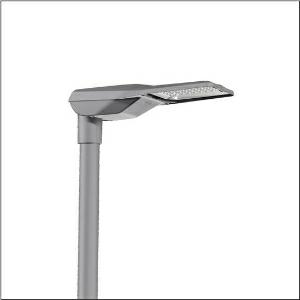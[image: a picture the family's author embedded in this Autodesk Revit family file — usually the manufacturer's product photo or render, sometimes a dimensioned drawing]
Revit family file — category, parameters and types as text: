
# Revit family: streetlight_sl_21_iq_mini___st1_0a_5xe2d31g08gb_f91a
name_source: partatom
category: Lighting Fixtures
units: mm (PartAtom-declared; Revit-internal decimal feet)

## family parameters
Cut with Voids When Loaded = No
Host = Face
Light Source = No
Part Type = Normal
Room Calculation Point = No
Round Connector Dimension = Use Diameter
Shared = No

## types (1)
- --- (1 x LED, 5680 lm, 37.1 W, 3000K)
    Apparent Load = 37 VA
    CIE Flux Codes = 37 72 97 100 100
    Color Rendering = 70
    Color Temperature = 3000K
    Default Elevation = 1800 mm
    Description = Streetlight SL 21 mini, mast luminaire, primary light control with lens, of PMMA, primary optical cover: cover, of toughened safety glass, transparent, light distribution: ST1.0a, light emission: direct distribution, primary light characteristic: asymmetric, installation type: post-top, side-entry, LED, High Power LED, rated luminous flux: 5.680lm, luminous efficacy: 153lm/W, light colour: 730, colour temperature: 3000K, control gear: ECG iQ, control: Street-Remote, Auto-Match, Temp-Guard, Lumen-Switch, Night-Set, Smart-Wire, Light-Fading, Desk-Remote (wireless, voltage-free reading and setting of iQ features in the workshop via application-optimized NFC function/RFID function), optimised constant luminous flux control (CLO 2.0), mains connection: 220..240V, AC, 50/60Hz, start of lifetime: 37W, end of lifetime: 39W, reduction: 18W, luminaire housing, of diecast aluminium, powder-coated, Siteco® metallic grey (DB 702S), corrosivity category C5 according to DIN EN ISO 12944, length: 628mm, width: 235mm, height: 110mm, spigot size: 60/76mm (post-top) and 42/60/76mm (side-entry), mast flange for spigot size: 42mm: 5XC10008XM4, 60mm: 5XC10008XM2, 76/60mm: 5XC10108XM1, protection rating (complete): IP66, insulation class (complete): insulation class II (safety insulation), certification: CE, ENEC, VDE, impact resistance: IK09, permissible operating ambient temperature for outdoor applications: -40..+50°C, standard-compliant lighting for roads and squares, packaging unit: 1 piece

Light Distribution: ST1.0a
    Height = 110 mm
    Lamp = 1 x LED
    Lamp Light Flux = 5680 lm
    Lamp Power = 37.1 W
    Lamp count = 1
    Length = 625 mm
    Luminous efficacy = 153 lm/W
    Manufacturer = Siteco
    ModVariant = No
    Model = 5XE2D31G08GB
    Number of Poles = 1
    OnlyDefault = Yes
    Power Factor = 1
    Product Name = Streetlight SL 21 iQ mini | ST1.0a
    Product group = mast luminaire | pylon top
    ProductGroupID = 6100
    Protection Class = Protection class II
    Protection Degree = IP 66
    RLX_Detail_Level = 1
    RlxData = <blob elided: 91865 chars, md5=34973ee0>
    Socket = socket
    Standby Power = 0 W
    System Light Flux = 5680 lm
    System Power = 37 W
    Type Comments = factory setting: luminous flux: 100 % | dim-lin: 254 | 385 mA
    Type Image = l_1003519.jpg
    URL = http://relux.com
    VarID = @adj_107187
    Voltage = 0 V
    Weight = 0.00 kg
    Width = 234 mm

## geometry (parser evidence)
native form markers: Blend x4, Sweep x10
no freeform markers — native parametric forms only
